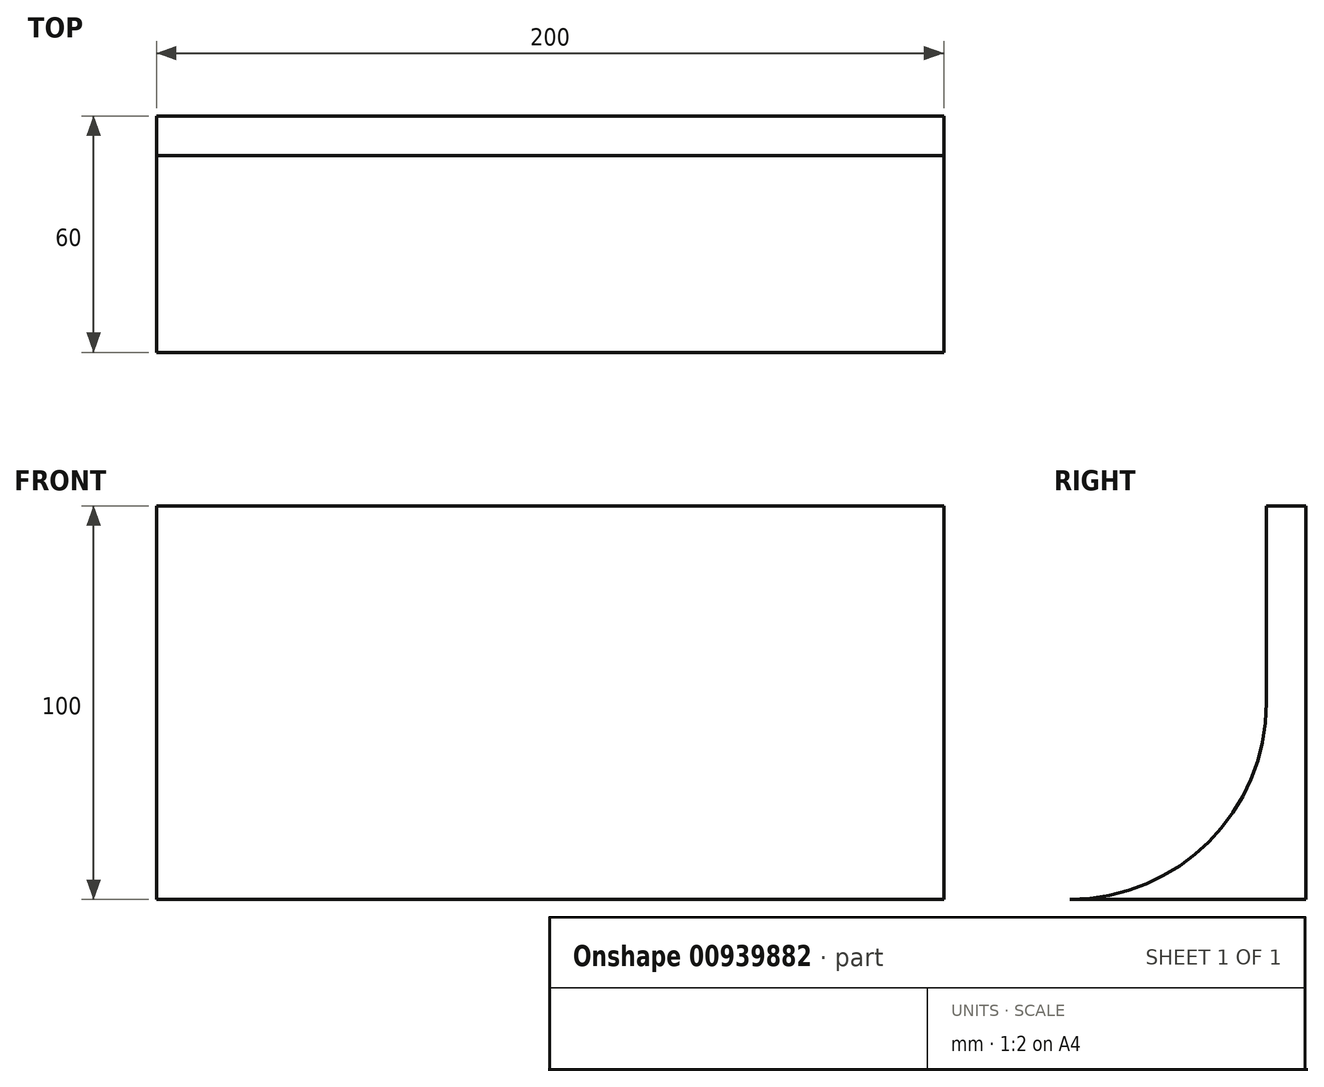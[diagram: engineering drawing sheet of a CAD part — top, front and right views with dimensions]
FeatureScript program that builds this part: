
annotation { "Feature Type Name" : "Feature", "Feature Type Description" : "" }
export const myFeature = defineFeature(function(context is Context, id is Id, definition is map)
    precondition{}
    {
        {
            var Q0;
            Q0=qCreatedBy(makeId("Top.planeOp"),FACE);
            var sketch = newSketch(context, id + "F0", { "sketchPlane" : qUnion([Q0])});
            skLineSegment(sketch, "E0.bottom", {"start": v(-100, 30) * mm, "end": v(100, 30) * mm});
            skLineSegment(sketch, "E0.top", {"start": v(-100, -30) * mm, "end": v(100, -30) * mm});
            skLineSegment(sketch, "E0.left", {"start": v(-100, 30) * mm, "end": v(-100, -30) * mm});
            skLineSegment(sketch, "E0.right", {"start": v(100, 30) * mm, "end": v(100, -30) * mm});
            skPoint(sketch, "E0.middle", {"position": v(0, 0) * mm});
            skSolve(sketch);
        }
        {
            var Q0;
            Q0 = qSketchRegion(id + "F0", true);
            extrude(context, id + "F1", {"entities" : qUnion([Q0]), "depth" : 100 * mm, "offsetDistance" : 25 * mm});
        }
        {
            var Q0;
            Q0=makeQuery(id+"F1.opExtrude","SWEPT_FACE",FACE,{"disambiguationData":[OSD([sQuery(id+"F0.wireOp",EDGE,"E0.left")])]});
            var sketch = newSketch(context, id + "F2", { "sketchPlane" : qUnion([Q0])});
            skLineSegment(sketch, "E1", {"start": v(-20, 100) * mm, "end": v(-20, 50) * mm});
            skArc(sketch, "E2", {"start": v(-20, 50) * mm, "mid": v(-5.36, 14.64) * mm, "end": v(30, 0) * mm});
            skLineSegment(sketch, "E3", {"start": v(-20, 100) * mm, "end": v(30, 100) * mm});
            skLineSegment(sketch, "E4", {"start": v(30, 100) * mm, "end": v(30, 0) * mm});
            skSolve(sketch);
        }
        {
            var Q0;
            Q0 = qSketchRegion(id + "F2", true);
            extrude(context, id + "F3", {"entities" : qUnion([Q0]), "operationType" : NewBodyOperationType.REMOVE, "oppositeDirection" : true, "depth" : 200 * mm, "offsetDistance" : 25 * mm});
        }
    });
